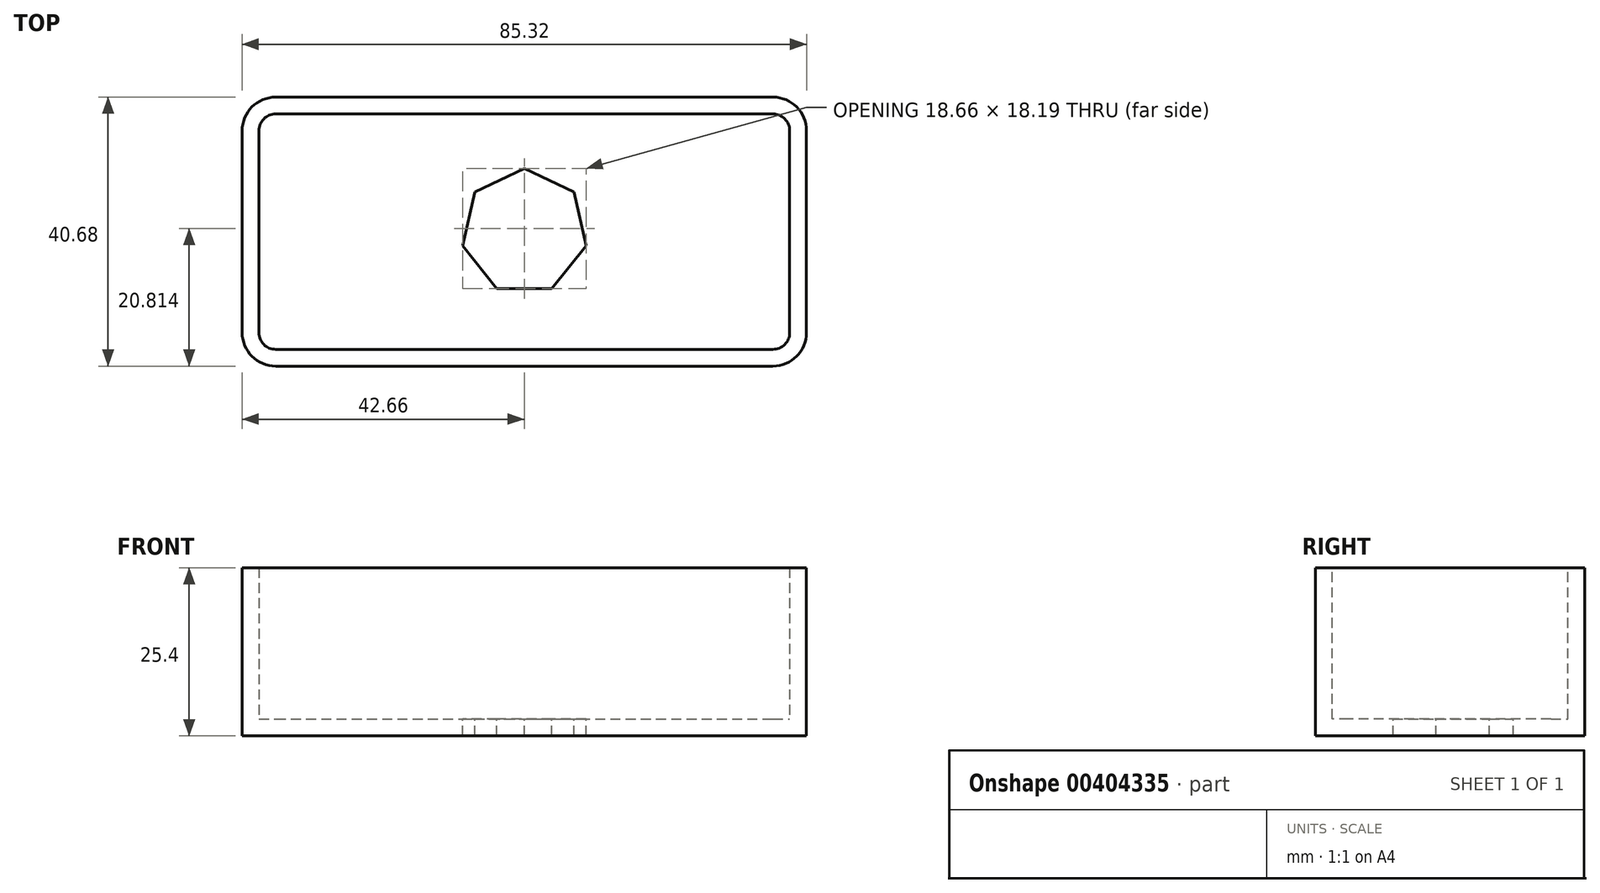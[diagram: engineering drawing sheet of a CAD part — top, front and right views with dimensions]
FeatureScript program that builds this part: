
annotation { "Feature Type Name" : "Feature", "Feature Type Description" : "" }
export const myFeature = defineFeature(function(context is Context, id is Id, definition is map)
    precondition{}
    {
        {
            var Q0;
            Q0=qCreatedBy(makeId("Top.planeOp"),FACE);
            var sketch = newSketch(context, id + "F0", { "sketchPlane" : qUnion([Q0])});
            skLineSegment(sketch, "E0.bottom", {"start": v(-42.66, 20.34) * mm, "end": v(42.66, 20.34) * mm});
            skLineSegment(sketch, "E0.top", {"start": v(-42.66, -20.34) * mm, "end": v(42.66, -20.34) * mm});
            skLineSegment(sketch, "E0.left", {"start": v(-42.66, 20.34) * mm, "end": v(-42.66, -20.34) * mm});
            skLineSegment(sketch, "E0.right", {"start": v(42.66, 20.34) * mm, "end": v(42.66, -20.34) * mm});
            skPoint(sketch, "E0.middle", {"position": v(0, 0) * mm});
            skSolve(sketch);
        }
        {
            var Q0;
            Q0 = qSketchRegion(id + "F0", true);
            extrude(context, id + "F1", {"entities" : qUnion([Q0]), "endBound" : BoundingType.SYMMETRIC, "depth" : 25.4 * mm});
        }
        {
            var Q0;
            Q0=makeQuery(id+"F1.opExtrude","SWEPT_EDGE",EDGE,{"disambiguationData":[OSD([sQuery(id+"F0.wireOp",EDGE,"E0.top"),sQuery(id+"F0.wireOp",EDGE,"E0.right")])]});
            var Q1;
            Q1=makeQuery(id+"F1.opExtrude","SWEPT_EDGE",EDGE,{"disambiguationData":[OSD([sQuery(id+"F0.wireOp",EDGE,"E0.bottom"),sQuery(id+"F0.wireOp",EDGE,"E0.right")])]});
            var Q2;
            Q2=makeQuery(id+"F1.opExtrude","SWEPT_EDGE",EDGE,{"disambiguationData":[OSD([sQuery(id+"F0.wireOp",EDGE,"E0.top"),sQuery(id+"F0.wireOp",EDGE,"E0.left")])]});
            var Q3;
            Q3=makeQuery(id+"F1.opExtrude","SWEPT_EDGE",EDGE,{"disambiguationData":[OSD([sQuery(id+"F0.wireOp",EDGE,"E0.bottom"),sQuery(id+"F0.wireOp",EDGE,"E0.left")])]});
            fillet(context, id + "F2", {"entities" : qUnion([Q0, Q1, Q2, Q3]), "radius" : 5.08 * mm, "tangentPropagation" : true, "allowEdgeOverflow" : false});
        }
        {
            var Q0;
            Q0=makeQuery(id+"F1.opExtrude","CAP_FACE",FACE,{"disambiguationData":[OSD([sQuery(id+"F0.wireOp",EDGE,"E0.bottom"),sQuery(id+"F0.wireOp",EDGE,"E0.top"),sQuery(id+"F0.wireOp",EDGE,"E0.left"),sQuery(id+"F0.wireOp",EDGE,"E0.right")])],"isStart":false});
            shell(context, id + "F3", {"entities" : qUnion([Q0]), "thickness" : 2.54 * mm});
        }
        {
            var Q0;
            Q0=makeQuery(id+"F3.opShell","OFFSET_FACE",FACE,{"disambiguationData":[OSD([sQuery(id+"F0.wireOp",EDGE,"E0.bottom"),sQuery(id+"F0.wireOp",EDGE,"E0.top"),sQuery(id+"F0.wireOp",EDGE,"E0.left"),sQuery(id+"F0.wireOp",EDGE,"E0.right")])]});
            var sketch = newSketch(context, id + "F4", { "sketchPlane" : qUnion([Q0])});
            skCircle(sketch, "E1.cCircle", {"center": v(0, 0) * mm, "radius": 8.62 * mm, "construction": true});
            skLineSegment(sketch, "E1.0", {"start": v(-9.33, -2.13) * mm, "end": v(-7.48, 5.97) * mm});
            skLineSegment(sketch, "E1.1", {"start": v(-7.48, 5.97) * mm, "end": v(0, 9.57) * mm});
            skLineSegment(sketch, "E1.2", {"start": v(0, 9.57) * mm, "end": v(7.48, 5.97) * mm});
            skLineSegment(sketch, "E1.3", {"start": v(7.48, 5.97) * mm, "end": v(9.33, -2.13) * mm});
            skLineSegment(sketch, "E1.4", {"start": v(9.33, -2.13) * mm, "end": v(4.15, -8.62) * mm});
            skLineSegment(sketch, "E1.5", {"start": v(4.15, -8.62) * mm, "end": v(-4.15, -8.62) * mm});
            skLineSegment(sketch, "E1.6", {"start": v(-4.15, -8.62) * mm, "end": v(-9.33, -2.13) * mm});
            skPoint(sketch, "E1.0.midPoint", {"position": v(-8.4, 1.92) * mm});
            skSolve(sketch);
        }
        {
            var Q0;
            Q0 = qSketchRegion(id + "F4", true);
            extrude(context, id + "F5", {"entities" : qUnion([Q0]), "operationType" : NewBodyOperationType.REMOVE, "endBound" : BoundingType.UP_TO_NEXT, "oppositeDirection" : true, "depth" : 25.4 * mm});
        }
    });
